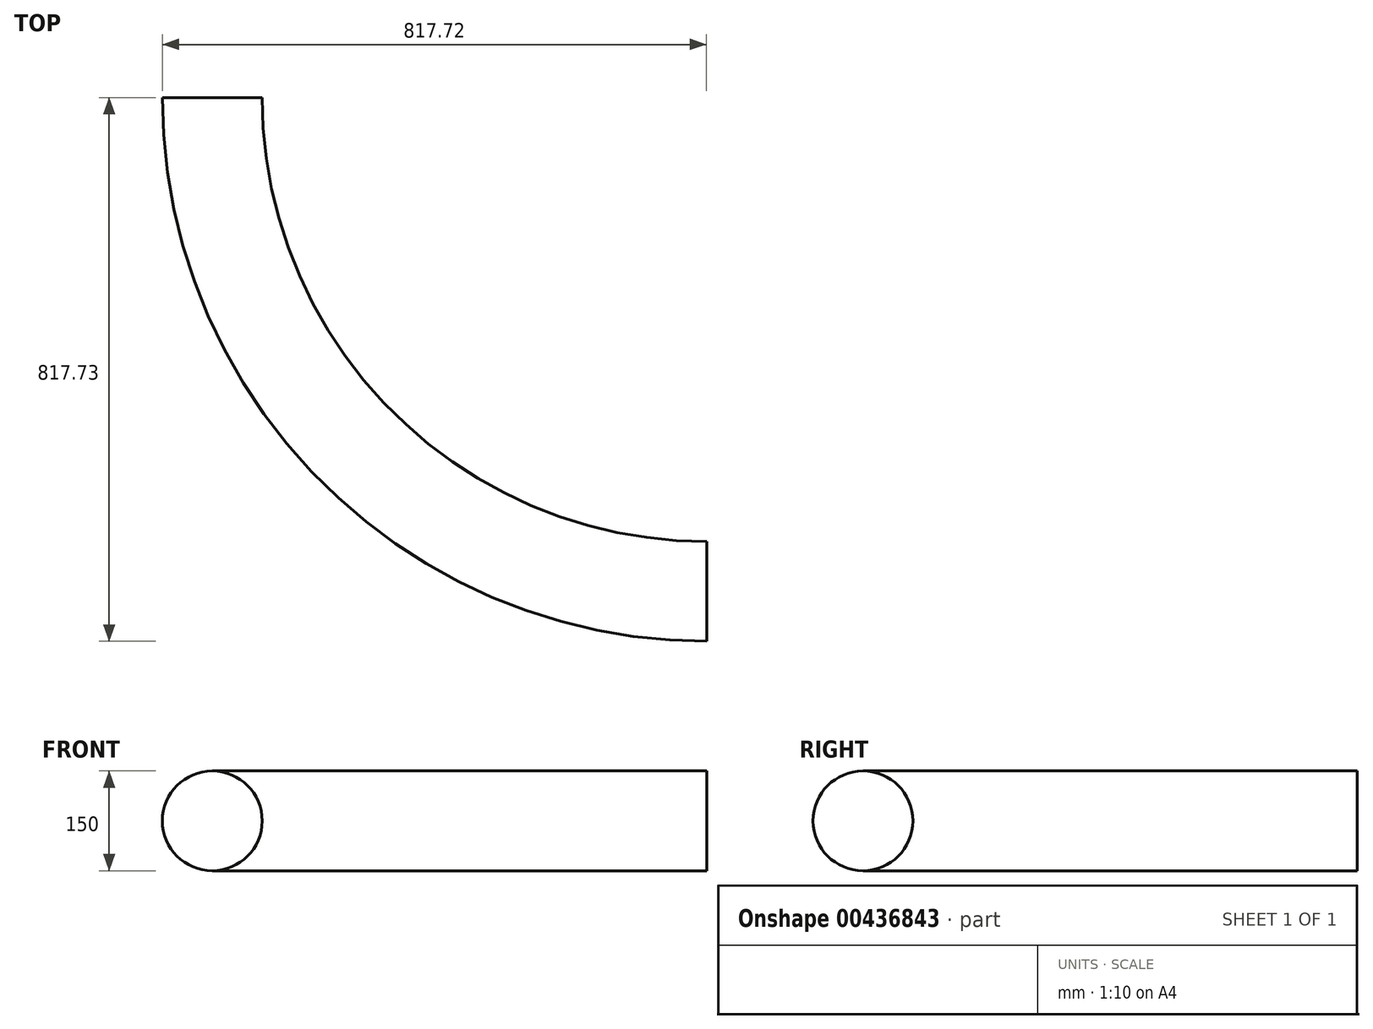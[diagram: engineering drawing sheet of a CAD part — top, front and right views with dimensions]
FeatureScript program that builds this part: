
annotation { "Feature Type Name" : "Feature", "Feature Type Description" : "" }
export const myFeature = defineFeature(function(context is Context, id is Id, definition is map)
    precondition{}
    {
        {
            var Q0;
            Q0=qCreatedBy(makeId("Front.planeOp"),FACE);
            var sketch = newSketch(context, id + "F0", { "sketchPlane" : qUnion([Q0])});
            skLineSegment(sketch, "E0", {"start": v(34.97, -615.44) * mm, "end": v(34.97, 891.44) * mm, "construction": true});
            skCircle(sketch, "E1", {"center": v(-707.75, 30.74) * mm, "radius": 75 * mm});
            skSolve(sketch);
        }
        {
            var Q0;
            Q0=makeQuery(id+"F0.imprint","IMPRINT",FACE,{"disambiguationData":[TD([[makeQuery(id+"F0.imprint","IMPRINT",EDGE,{"derivedFrom":sQuery(id+"F0.wireOp",EDGE,"E1")}),1.0]])]});
            var Q1;
            Q1=sQuery(id+"F0.wireOp",EDGE,"E0");
            revolve(context, id + "F1", {"entities" : qUnion([Q0]), "axis" : qUnion([Q1]), "revolveType" : RevolveType.ONE_DIRECTION, "angle" : 90 * degree});
        }
    });
